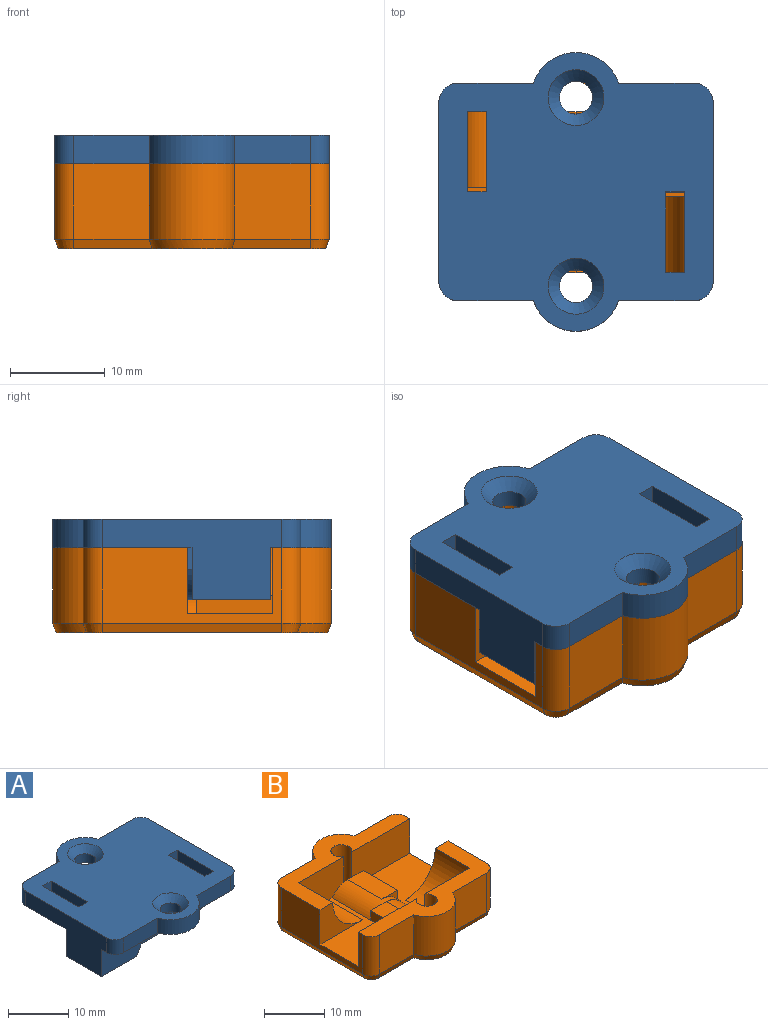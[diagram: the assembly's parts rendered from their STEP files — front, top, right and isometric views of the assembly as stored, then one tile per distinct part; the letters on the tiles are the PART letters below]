
ASSEMBLY  parts=2 mates=1
PART A: 44 faces, bbox 29x29.4x8.5 mm
  f0: plane 0.67x0.03mm, normal (0,0,1), area 0mm2, adj f11,f34
  f1: plane 8.5x8.35mm, normal (0,1,0), area 37.9mm2, adj f8,f9,f10,f14,f22,f35,f39,f40
  f2: plane 5.04x1.94mm, normal (0,1,0), area 4.7mm2, adj f4,f5,f6,f7,f17
  f3: plane 0.67x0.03mm, normal (0,0,1), area 0mm2, adj f20,f38
  f4: cylinder r=5.5mm len=8.25mm, axis (0,-1,0), area 51.8mm2, adj f2,f5,f11,f12,f41
  f5: plane 8.25x0.22mm, normal (0,0,-1), area 1.9mm2, adj f2,f4,f6,f11
  f6: cylinder r=7.66mm len=8.25mm, axis (0,-1,0), area 38.4mm2, adj f2,f5,f7,f11
  f7: plane 16.5x10.28mm, normal (0,0,-1), area 85.7mm2, adj f2,f6,f8,f11,f16,f17,f19,f20
  f8: plane 8.25x1.94mm, normal (0.86,0,-0.51), area 18.6mm2, adj f1,f7,f9,f11,f19
  f9: plane 8.25x8.2mm, normal (0,0,-1), area 67.7mm2, adj f1,f8,f10,f11
  f10: plane 19x8.5mm, normal (-1,0,0), area 102.4mm2, adj f1,f9,f11,f21,f22,f29,f30,f39
  f11: plane 23.97x5.5mm, normal (0,-1,0), area 110.9mm2, adj f0,f4,f5,f6,f7,f8,f9,f10
  f12: plane 9.34x8.5mm, normal (0,-1,0), area 38mm2, adj f4,f13,f17,f18,f21,f37,f39,f41
  f13: plane 19x8.5mm, normal (1,0,0), area 102.4mm2, adj f12,f18,f20,f21,f22,f24,f25,f39
  f14: cylinder r=5.5mm len=8.25mm, axis (0,1,0), area 51.8mm2, adj f1,f15,f19,f20,f40
  f15: plane 8.25x0.12mm, normal (0,0,-1), area 1mm2, adj f14,f16,f19,f20
  f16: cylinder r=5.89mm len=8.25mm, axis (0,1,0), area 40.6mm2, adj f7,f15,f19,f20
  f17: plane 8.25x1.94mm, normal (-1,0,0), area 16mm2, adj f2,f7,f12,f18,f20
  f18: plane 9.34x8.25mm, normal (0,0,-1), area 77.1mm2, adj f12,f13,f17,f20
  f19: plane 6.14x1.94mm, normal (0,-1,0), area 5.1mm2, adj f7,f8,f14,f15,f16
  f20: plane 23.97x5.5mm, normal (0,1,0), area 111.5mm2, adj f3,f7,f13,f14,f15,f16,f17,f18
  f21: plane 28.97x14.72mm, normal (0,0,-1), area 128.3mm2, adj f10,f11,f12,f13,f24,f30,f31,f32
  f22: plane 28.97x14.72mm, normal (0,0,-1), area 128.3mm2, adj f1,f10,f13,f20,f23,f25,f26,f27
  f23: plane 3x2mm, normal (0,-1,0), area 6mm2, adj f22,f35,f39,f40
  f24: cylinder r=2mm len=3mm, axis (0,0,-1), area 9.4mm2, adj f13,f21,f36,f39
  f25: cylinder r=2mm len=3mm, axis (0,0,-1), area 9.4mm2, adj f13,f22,f26,f39
  f26: plane 7.99x3mm, normal (0,1,0), area 24mm2, adj f22,f25,f27,f39
  f27: cylinder r=4.75mm len=9mm, axis (0,0,-1), area 35.4mm2, adj f22,f26,f28,f39
  f28: plane 7.99x3mm, normal (0,1,0), area 24mm2, adj f22,f27,f29,f39
  f29: cylinder r=2mm len=3mm, axis (0,0,-1), area 9.4mm2, adj f10,f22,f28,f39
  f30: cylinder r=2mm len=3mm, axis (0,0,-1), area 9.4mm2, adj f10,f21,f31,f39
  f31: plane 7.99x3mm, normal (0,-1,0), area 24mm2, adj f21,f30,f32,f39
  f32: cylinder r=4.75mm len=9mm, axis (0,0,-1), area 35.4mm2, adj f21,f31,f36,f39
  f33: plane 3x2mm, normal (0,1,0), area 6mm2, adj f21,f37,f39,f41
  f34: cylinder r=1.75mm len=3.5mm, axis (0,0,-1), area 19.8mm2, adj f0,f21,f42
  f35: plane 8.5x3mm, normal (1,0,0), area 25.5mm2, adj f1,f22,f23,f39
  f36: plane 7.99x3mm, normal (0,-1,0), area 24mm2, adj f21,f24,f32,f39
  f37: plane 8.5x3mm, normal (-1,0,0), area 25.5mm2, adj f12,f21,f33,f39
  f38: cylinder r=1.75mm len=3.5mm, axis (0,0,-1), area 19.8mm2, adj f3,f22,f43
  f39: plane 29.44x28.97mm, normal (0,0,1), area 616.6mm2, adj f1,f10,f12,f13,f23,f24,f25,f26
  f40: plane 8.5x5.29mm, normal (-1,0,0), area 44.4mm2, adj f1,f14,f20,f22,f23,f39
  f41: plane 8.5x5.29mm, normal (1,0,0), area 44.4mm2, adj f4,f11,f12,f21,f33,f39
  f42: cone r=1.75mm half-angle=45deg, axis (0,0,1), area 25.1mm2, adj f34,f39
  f43: cone r=1.75mm half-angle=45deg, axis (0,0,1), area 25.1mm2, adj f38,f39
PART B: 54 faces, bbox 29x29.5x9 mm
  f0: plane 17x10.84mm, normal (0,0,1), area 104.3mm2, adj f1,f10,f16,f18,f19,f30,f34
  f1: plane 13.53x7mm, normal (0,1,0), area 89.5mm2, adj f0,f5,f10,f17,f34,f35
  f2: plane 10.53x7mm, normal (0,1,0), area 60.5mm2, adj f3,f5,f17,f20,f36
  f3: plane 17x10.84mm, normal (0,0,1), area 104.3mm2, adj f2,f6,f14,f20,f21,f28,f30,f36
  f4: plane 28.97x14.22mm, normal (0,0,1), area 121.1mm2, adj f6,f7,f8,f9,f10,f14,f15,f16
  f5: plane 28.97x14.22mm, normal (0,0,1), area 121.1mm2, adj f1,f2,f6,f10,f11,f12,f13,f17
  f6: plane 19x8mm, normal (1,0,0), area 89mm2, adj f3,f4,f5,f14,f21,f24,f25,f44
  f7: plane 8x7.99mm, normal (0,1,0), area 63.9mm2, adj f4,f8,f25,f48
  f8: cylinder r=4.75mm len=9mm, axis (0,0,-1), area 94.5mm2, adj f4,f7,f9,f50
  f9: plane 8x7.99mm, normal (0,1,0), area 63.9mm2, adj f4,f8,f26,f51
  f10: plane 19x8mm, normal (-1,0,0), area 89mm2, adj f0,f1,f4,f5,f19,f23,f26,f47
  f11: plane 8x7.99mm, normal (0,-1,0), area 63.9mm2, adj f5,f12,f23,f43
  f12: cylinder r=4.75mm len=9mm, axis (0,0,-1), area 94.5mm2, adj f5,f11,f13,f41
  f13: plane 8x7.99mm, normal (0,-1,0), area 63.9mm2, adj f5,f12,f24,f40
  f14: plane 13.53x7mm, normal (0,-1,0), area 89.5mm2, adj f3,f4,f6,f15,f28,f29
  f15: cylinder r=1.75mm len=8mm, axis (0,0,-1), area 73.9mm2, adj f4,f14,f16,f27,f32,f53
  f16: plane 10.53x7mm, normal (0,-1,0), area 60.1mm2, adj f0,f4,f15,f18,f30
  f17: cylinder r=1.75mm len=8mm, axis (0,0,-1), area 73.9mm2, adj f1,f2,f5,f33,f38,f52
  f18: cylinder r=7mm len=8mm, axis (0,1,0), area 88mm2, adj f0,f4,f16,f19
  f19: plane 10x7mm, normal (0,-1,0), area 31.5mm2, adj f0,f4,f10,f18
  f20: cylinder r=7mm len=8mm, axis (0,-1,0), area 88mm2, adj f2,f3,f5,f21
  f21: plane 10x7mm, normal (0,1,0), area 31.5mm2, adj f3,f5,f6,f20
  f22: plane 28.71x28.24mm, normal (0,0,-1), area 638.9mm2, adj f40,f41,f42,f43,f44,f45,f46,f47
  f23: cylinder r=2mm len=8mm, axis (0,0,-1), area 25.1mm2, adj f5,f10,f11,f45
  f24: cylinder r=2mm len=8mm, axis (0,0,-1), area 25.1mm2, adj f5,f6,f13,f42
  f25: cylinder r=2mm len=8mm, axis (0,0,-1), area 25.1mm2, adj f4,f6,f7,f46
  f26: cylinder r=2mm len=8mm, axis (0,0,-1), area 25.1mm2, adj f4,f9,f10,f49
  f27: plane 1.91x0.28mm, normal (0,0,-1), area 0.4mm2, adj f15,f32
  f28: plane 8x1.94mm, normal (1,0,0), area 15.5mm2, adj f3,f14,f29,f31
  f29: plane 8x3.64mm, normal (0,0,1), area 29.1mm2, adj f14,f28,f30,f31,f32
  f30: cylinder r=4.39mm len=9mm, axis (0,1,0), area 43mm2, adj f0,f3,f16,f29,f31,f32,f37,f39
  f31: plane 3.64x1.94mm, normal (0,-1,0), area 2.1mm2, adj f28,f29,f30
  f32: plane 1.94x1.91mm, normal (0,1,0), area 3.7mm2, adj f15,f27,f29,f30
  f33: plane 1.91x0.28mm, normal (0,0,-1), area 0.4mm2, adj f17,f38
  f34: plane 8x1.94mm, normal (-1,0,0), area 15.5mm2, adj f0,f1,f35,f37
  f35: plane 8x3.64mm, normal (0,0,1), area 29.1mm2, adj f1,f34,f36,f37,f38
  f36: cylinder r=6.16mm len=8mm, axis (0,-1,0), area 33.7mm2, adj f2,f3,f35,f38,f39
  f37: plane 3.64x1.94mm, normal (0,1,0), area 2.1mm2, adj f30,f34,f35
  f38: plane 1.94x1.91mm, normal (0,-1,0), area 3.6mm2, adj f17,f33,f35,f36
  f39: plane 3.64x1.94mm, normal (0,-1,0), area 0.5mm2, adj f30,f36
  f40: plane 8.26x1.01mm, normal (0,-0.94,-0.34), area 8.6mm2, adj f13,f22,f41,f42
  f41: cone r=4.39mm half-angle=20deg, axis (0,0,1), area 12.4mm2, adj f12,f22,f40,f43
  f42: cone r=1.64mm half-angle=20deg, axis (0,0,1), area 3mm2, adj f22,f24,f40,f44
  f43: plane 8.26x1.01mm, normal (0,-0.94,-0.34), area 8.6mm2, adj f11,f22,f41,f45
  f44: plane 19x1mm, normal (0.94,0,-0.34), area 20.2mm2, adj f6,f22,f42,f46
  f45: cone r=1.64mm half-angle=20deg, axis (0,0,1), area 3mm2, adj f22,f23,f43,f47
  f46: cone r=1.64mm half-angle=20deg, axis (0,0,1), area 3mm2, adj f22,f25,f44,f48
  f47: plane 19x1mm, normal (-0.94,0,-0.34), area 20.2mm2, adj f10,f22,f45,f49
  f48: plane 8.26x1.01mm, normal (0,0.94,-0.34), area 8.6mm2, adj f7,f22,f46,f50
  f49: cone r=1.64mm half-angle=20deg, axis (0,0,1), area 3mm2, adj f22,f26,f47,f51
  f50: cone r=4.39mm half-angle=20deg, axis (0,0,1), area 12.4mm2, adj f8,f22,f48,f51
  f51: plane 8.26x1.01mm, normal (0,0.94,-0.34), area 8.6mm2, adj f9,f22,f49,f50
  f52: cone r=1.75mm half-angle=20deg, axis (0,0,-1), area 12.9mm2, adj f17,f22
  f53: cone r=1.75mm half-angle=20deg, axis (0,0,-1), area 12.9mm2, adj f15,f22
PLACE A t=(0.41,10.15,7.69)mm
PLACE B t=(0.41,10.15,7.69)mm
MATE fastened B.f12 <-> A.f32  axis (0,0,1) through (-0.18,-1.11,14.69)mm
